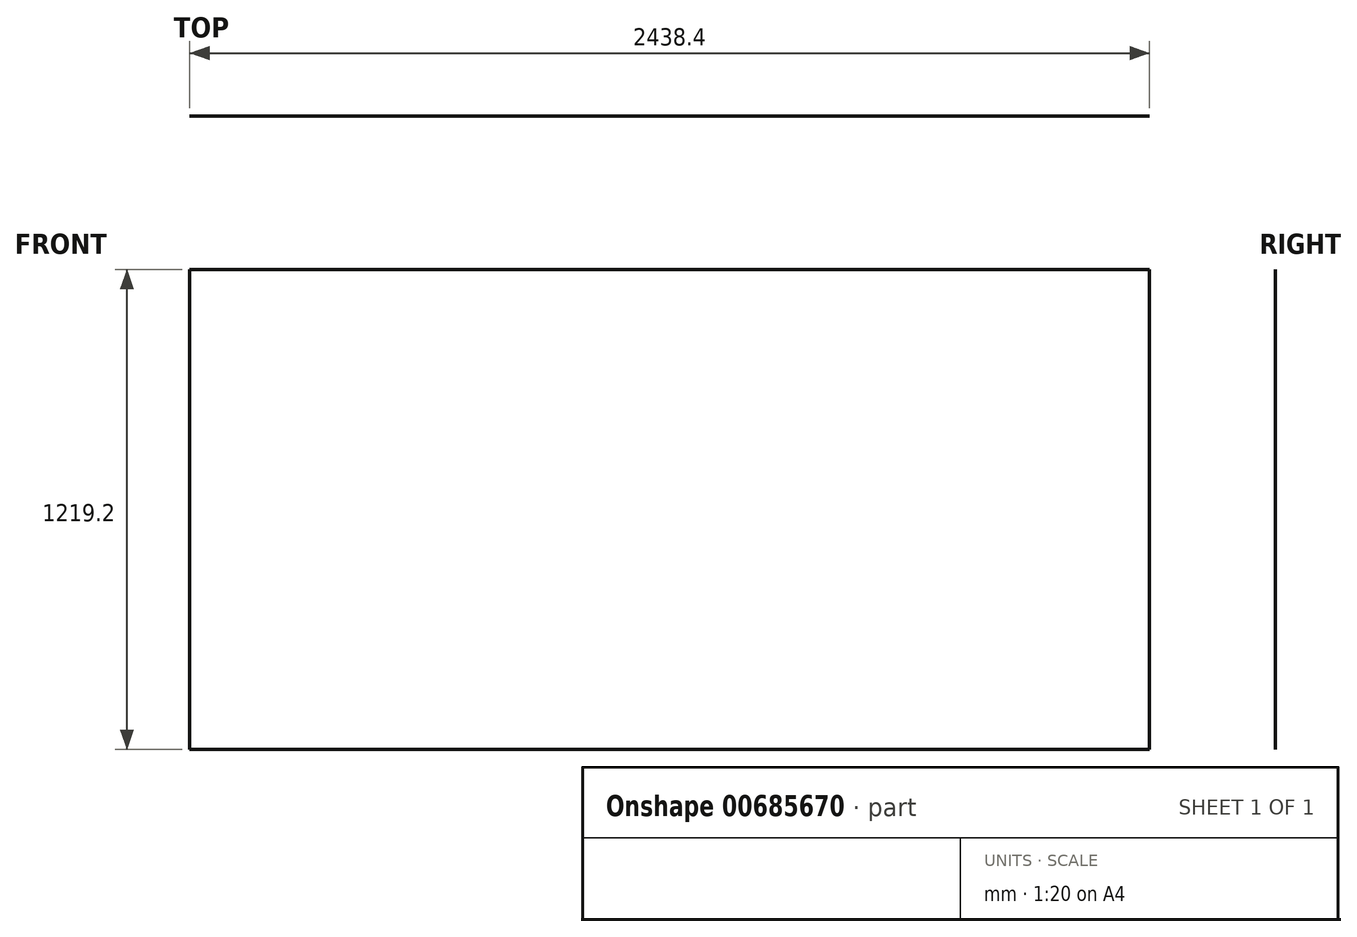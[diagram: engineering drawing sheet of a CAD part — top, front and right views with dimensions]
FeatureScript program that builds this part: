
annotation { "Feature Type Name" : "Feature", "Feature Type Description" : "" }
export const myFeature = defineFeature(function(context is Context, id is Id, definition is map)
    precondition{}
    {
        {
            var Q0;
            Q0=qCreatedBy(makeId("Front.planeOp"),FACE);
            var sketch = newSketch(context, id + "F0", { "sketchPlane" : qUnion([Q0])});
            skLineSegment(sketch, "E0.bottom", {"start": v(0, 0) * mm, "end": v(2438.4, 0) * mm});
            skLineSegment(sketch, "E0.top", {"start": v(0, 1219.2) * mm, "end": v(2438.4, 1219.2) * mm});
            skLineSegment(sketch, "E0.left", {"start": v(0, 0) * mm, "end": v(0, 1219.2) * mm});
            skLineSegment(sketch, "E0.right", {"start": v(2438.4, 0) * mm, "end": v(2438.4, 1219.2) * mm});
            skSolve(sketch);
        }
        {
            var Q0;
            Q0 = qSketchRegion(id + "F0", true);
            extrude(context, id + "F1", {"entities" : qUnion([Q0]), "depth" : .25 / 3657.6 * mm, "offsetDistance" : 30.48 * mm});
        }
    });
